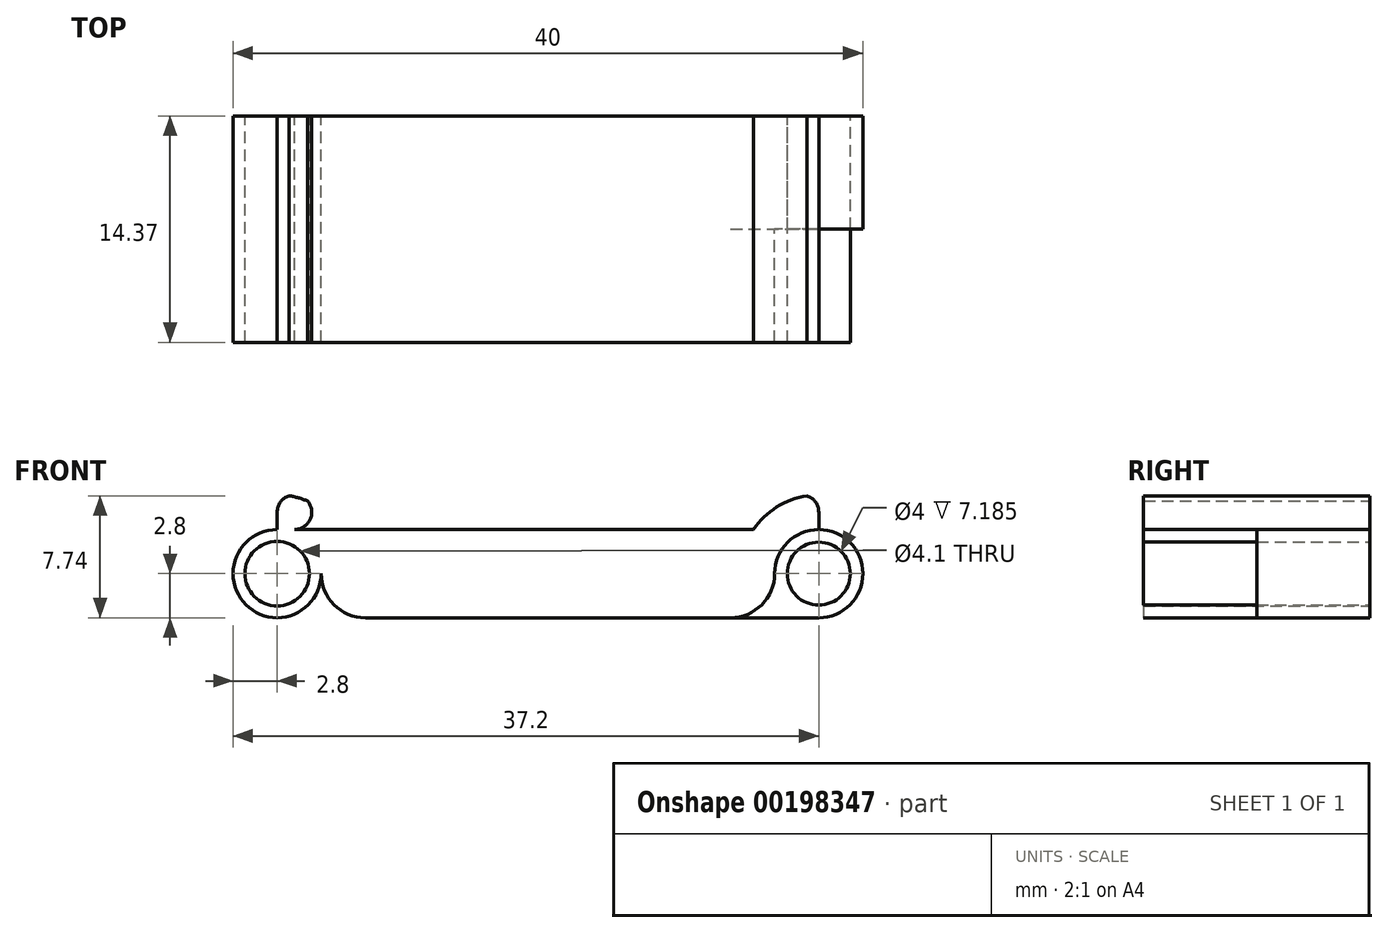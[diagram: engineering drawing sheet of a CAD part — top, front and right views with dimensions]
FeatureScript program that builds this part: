
annotation { "Feature Type Name" : "Feature", "Feature Type Description" : "" }
export const myFeature = defineFeature(function(context is Context, id is Id, definition is map)
    precondition{}
    {
        {
            var Q0;
            Q0=qCreatedBy(makeId("Front.planeOp"),FACE);
            var sketch = newSketch(context, id + "F0", { "sketchPlane" : qUnion([Q0])});
            skLineSegment(sketch, "E0.bottom", {"start": v(2.8, 0) * mm, "end": v(40, 0) * mm});
            skLineSegment(sketch, "E0.top", {"start": v(3.9, 5.6) * mm, "end": v(36.1, 5.6) * mm});
            skLineSegment(sketch, "E1.bottom", {"start": v(36.1, 5.6) * mm, "end": v(34.4, 5.6) * mm, "construction": true});
            skLineSegment(sketch, "E1.top", {"start": v(37.2, 0) * mm, "end": v(34.4, 0) * mm, "construction": true});
            skLineSegment(sketch, "E1.right", {"start": v(34.4, 5.6) * mm, "end": v(34.4, 0) * mm, "construction": true});
            skLineSegment(sketch, "E2", {"start": v(34.4, 5.6) * mm, "end": v(40, 0) * mm, "construction": true});
            skCircle(sketch, "E3", {"center": v(37.2, 2.8) * mm, "radius": 2.8 * mm});
            skCircle(sketch, "E4", {"center": v(37.2, 2.8) * mm, "radius": 2 * mm});
            skArc(sketch, "E5", {"start": v(37.2, 7.8) * mm, "mid": v(34.85, 7.22) * mm, "end": v(33.06, 5.6) * mm});
            skLineSegment(sketch, "E6", {"start": v(37.2, 2.8) * mm, "end": v(37.2, 7.8) * mm, "construction": true});
            skPoint(sketch, "E6.endSnap0", {"position": v(37.2, 5.6) * mm});
            skLineSegment(sketch, "E7", {"start": v(37.2, 7.8) * mm, "end": v(37.2, 5.6) * mm, "construction": true});
            skCircle(sketch, "E8", {"center": v(37.2, 6.7) * mm, "radius": 1.1 * mm, "construction": true});
            skLineSegment(sketch, "E9", {"start": v(37.2, 6.7) * mm, "end": v(36.1, 6.7) * mm, "construction": true});
            skArc(sketch, "E10", {"start": v(35.26, 7.4) * mm, "mid": v(35.1, 6.24) * mm, "end": v(36.1, 5.6) * mm});
            skCircle(sketch, "E11", {"center": v(34.4, 2.8) * mm, "radius": 2.8 * mm, "construction": true});
            skArc(sketch, "E12", {"start": v(31.6, 0) * mm, "mid": v(33.58, 0.82) * mm, "end": v(34.4, 2.8) * mm});
            skLineSegment(sketch, "E13", {"start": v(20, 5.6) * mm, "end": v(20, 0) * mm, "construction": true});
            skLineSegment(sketch, "E14.MirrorCS", {"start": v(2.8, 7.8) * mm, "end": v(2.8, 5.6) * mm, "construction": true});
            skLineSegment(sketch, "E15.MirrorCS", {"start": v(2.8, 6.7) * mm, "end": v(3.9, 6.7) * mm, "construction": true});
            skArc(sketch, "E16.MirrorC", {"start": v(4.74, 7.4) * mm, "mid": v(4.9, 6.24) * mm, "end": v(3.9, 5.6) * mm});
            skArc(sketch, "E17.MirrorC", {"start": v(8.4, 0) * mm, "mid": v(6.42, 0.82) * mm, "end": v(5.6, 2.8) * mm});
            skCircle(sketch, "E18.MirrorC", {"center": v(5.6, 2.8) * mm, "radius": 2.8 * mm, "construction": true});
            skLineSegment(sketch, "E19.MirrorCS", {"start": v(5.6, 5.6) * mm, "end": v(0, 0) * mm, "construction": true});
            skCircle(sketch, "E20.MirrorC", {"center": v(2.8, 2.8) * mm, "radius": 2.8 * mm});
            skLineSegment(sketch, "E21.MirrorCS", {"start": v(5.6, 5.6) * mm, "end": v(5.6, 0) * mm, "construction": true});
            skLineSegment(sketch, "E22.MirrorCS", {"start": v(2.8, 2.8) * mm, "end": v(2.8, 7.8) * mm, "construction": true});
            skCircle(sketch, "E23.MirrorC", {"center": v(2.8, 6.7) * mm, "radius": 1.1 * mm, "construction": true});
            skLineSegment(sketch, "E24.MirrorCS", {"start": v(37.2, 0) * mm, "end": v(2.8, 0) * mm});
            skLineSegment(sketch, "E25.MirrorCS", {"start": v(36.1, 5.6) * mm, "end": v(3.9, 5.6) * mm});
            skPoint(sketch, "E26.MirrorP", {"position": v(2.8, 5.6) * mm});
            skLineSegment(sketch, "E27.MirrorCS", {"start": v(3.9, 5.6) * mm, "end": v(5.6, 5.6) * mm, "construction": true});
            skLineSegment(sketch, "E28.MirrorCS", {"start": v(2.8, 0) * mm, "end": v(5.6, 0) * mm, "construction": true});
            skPoint(sketch, "E29.orphan", {"position": v(40, 0) * mm});
            skPoint(sketch, "E30.orphan", {"position": v(40, 5.6) * mm});
            skArc(sketch, "E31.trimOffspring", {"start": v(3.55, 7.74) * mm, "mid": v(5.47, 7.03) * mm, "end": v(6.94, 5.6) * mm});
            skPoint(sketch, "E32.orphan", {"position": v(0, 5.6) * mm});
            skPoint(sketch, "E33.orphan", {"position": v(0, 0) * mm});
            skArc(sketch, "E34.trimOffspring", {"start": v(37.2, 6.7) * mm, "mid": v(37, 7.34) * mm, "end": v(36.45, 7.74) * mm});
            skLineSegment(sketch, "E35.trimOffspring", {"start": v(37.2, 5.6) * mm, "end": v(40, 5.6) * mm});
            skLineSegment(sketch, "E36", {"start": v(37.2, 6.7) * mm, "end": v(37.2, 5.6) * mm});
            skArc(sketch, "E37.trimOffspring", {"start": v(2.8, 6.7) * mm, "mid": v(3, 7.34) * mm, "end": v(3.55, 7.74) * mm});
            skLineSegment(sketch, "E38", {"start": v(2.8, 6.7) * mm, "end": v(2.8, 5.6) * mm});
            skCircle(sketch, "E39", {"center": v(2.8, 2.8) * mm, "radius": 2.05 * mm});
            skSolve(sketch);
        }
        {
            var Q0;
            Q0=makeQuery(id+"F0.imprint","IMPRINT",FACE,{"disambiguationData":[TD([[makeQuery(id+"F0.imprint","IMPRINT",EDGE,{"derivedFrom":sQuery(id+"F0.wireOp",EDGE,"E4")}),1.0]])]});
            extrude(context, id + "F1", {"entities" : qUnion([Q0]), "depth" : 14.37 * mm});
        }
        {
            var Q0;
            {var subQ1=sQuery(id+"F0.wireOp",EDGE,"E12");Q0=makeQuery(id+"F0.imprint","IMPRINT",FACE,{"disambiguationData":[TD([[makeQuery(id+"F0.imprint","IMPRINT",EDGE,{"derivedFrom":subQ1}),1.0]])]});}
            var Q1;
            {var subQ0=sQuery(id+"F0.wireOp",EDGE,"E10");var subQ1=sQuery(id+"F0.wireOp",EDGE,"E5");var subQ2=makeQuery(id+"F0.imprint","INTERSECT",VERTEX,{"disambiguationData":[OD(0.0)],"derivedFrom":[subQ1,subQ0]});Q1=makeQuery(id+"F0.imprint","IMPRINT",FACE,{"disambiguationData":[TD([[makeQuery(id+"F0.imprint","IMPRINT",EDGE,{"disambiguationData":[TD([[subQ2,1.0]])],"derivedFrom":subQ1}),1.0]])]});}
            var Q2;
            {var subQ0=sQuery(id+"F0.wireOp",EDGE,"E25.MirrorCS");var subQ1=sQuery(id+"F0.wireOp",EDGE,"E5");var subQ2=makeQuery(id+"F0.imprint","INTERSECT",VERTEX,{"derivedFrom":[subQ1,subQ0]});Q2=makeQuery(id+"F0.imprint","IMPRINT",FACE,{"disambiguationData":[TD([[makeQuery(id+"F0.imprint","IMPRINT",EDGE,{"disambiguationData":[TD([[subQ2,1.0]])],"derivedFrom":subQ1}),1.0]])]});}
            var Q3;
            {var subQ0=sQuery(id+"F0.wireOp",EDGE,"E31.trimOffspring");var subQ1=sQuery(id+"F0.wireOp",EDGE,"E16.MirrorC");var subQ2=makeQuery(id+"F0.imprint","INTERSECT",VERTEX,{"disambiguationData":[OD(0.0)],"derivedFrom":[subQ1,subQ0]});Q3=makeQuery(id+"F0.imprint","IMPRINT",FACE,{"disambiguationData":[TD([[makeQuery(id+"F0.imprint","IMPRINT",EDGE,{"disambiguationData":[TD([[subQ2,-1.0]])],"derivedFrom":subQ0}),-1.0]])]});}
            var Q4;
            {var subQ0=sQuery(id+"F0.wireOp",EDGE,"E31.trimOffspring");var subQ1=sQuery(id+"F0.wireOp",EDGE,"E16.MirrorC");var subQ2=makeQuery(id+"F0.imprint","INTERSECT",VERTEX,{"disambiguationData":[OD(0.0)],"derivedFrom":[subQ1,subQ0]});Q4=makeQuery(id+"F0.imprint","IMPRINT",FACE,{"disambiguationData":[TD([[makeQuery(id+"F0.imprint","IMPRINT",EDGE,{"disambiguationData":[TD([[subQ2,1.0]])],"derivedFrom":subQ0}),-1.0]])]});}
            var Q5;
            Q5=makeQuery(id+"F0.imprint","IMPRINT",FACE,{"disambiguationData":[TD([[makeQuery(id+"F0.imprint","IMPRINT",EDGE,{"derivedFrom":sQuery(id+"F0.wireOp",EDGE,"E152.MirrorC")}),1.0]])]});
            extrude(context, id + "F2", {"entities" : qUnion([Q0, Q1, Q2, Q3, Q4, Q5]), "depth" : 14.37 * mm});
        }
        {
            var Q0;
            Q0=makeQuery(id+"F0.imprint","IMPRINT",FACE,{"disambiguationData":[TD([[makeQuery(id+"F0.imprint","IMPRINT",EDGE,{"derivedFrom":sQuery(id+"F0.wireOp",EDGE,"E4")}),-1.0]])]});
            var Q1;
            {var subQ3=sQuery(id+"F0.wireOp",EDGE,"E12");Q1=makeQuery(id+"F0.imprint","IMPRINT",FACE,{"disambiguationData":[TD([[makeQuery(id+"F0.imprint","IMPRINT",EDGE,{"derivedFrom":subQ3}),-1.0]])]});}
            extrude(context, id + "F3", {"entities" : qUnion([Q0, Q1]), "depth" : 7.18 * mm});
        }
        {
            var Q0;
            {var subQ0=sQuery(id+"F0.wireOp",EDGE,"E17.MirrorC");Q0=makeQuery(id+"F0.imprint","IMPRINT",FACE,{"disambiguationData":[TD([[makeQuery(id+"F0.imprint","IMPRINT",EDGE,{"derivedFrom":subQ0}),1.0]])]});}
            var Q1;
            Q1=makeQuery(id+"F0.imprint","IMPRINT",FACE,{"disambiguationData":[TD([[makeQuery(id+"F0.imprint","IMPRINT",EDGE,{"derivedFrom":sQuery(id+"F0.wireOp",EDGE,"E39")}),-1.0]])]});
            extrude(context, id + "F4", {"entities" : qUnion([Q0, Q1]), "operationType" : NewBodyOperationType.ADD, "depth" : 14.37 * mm});
        }
    });
